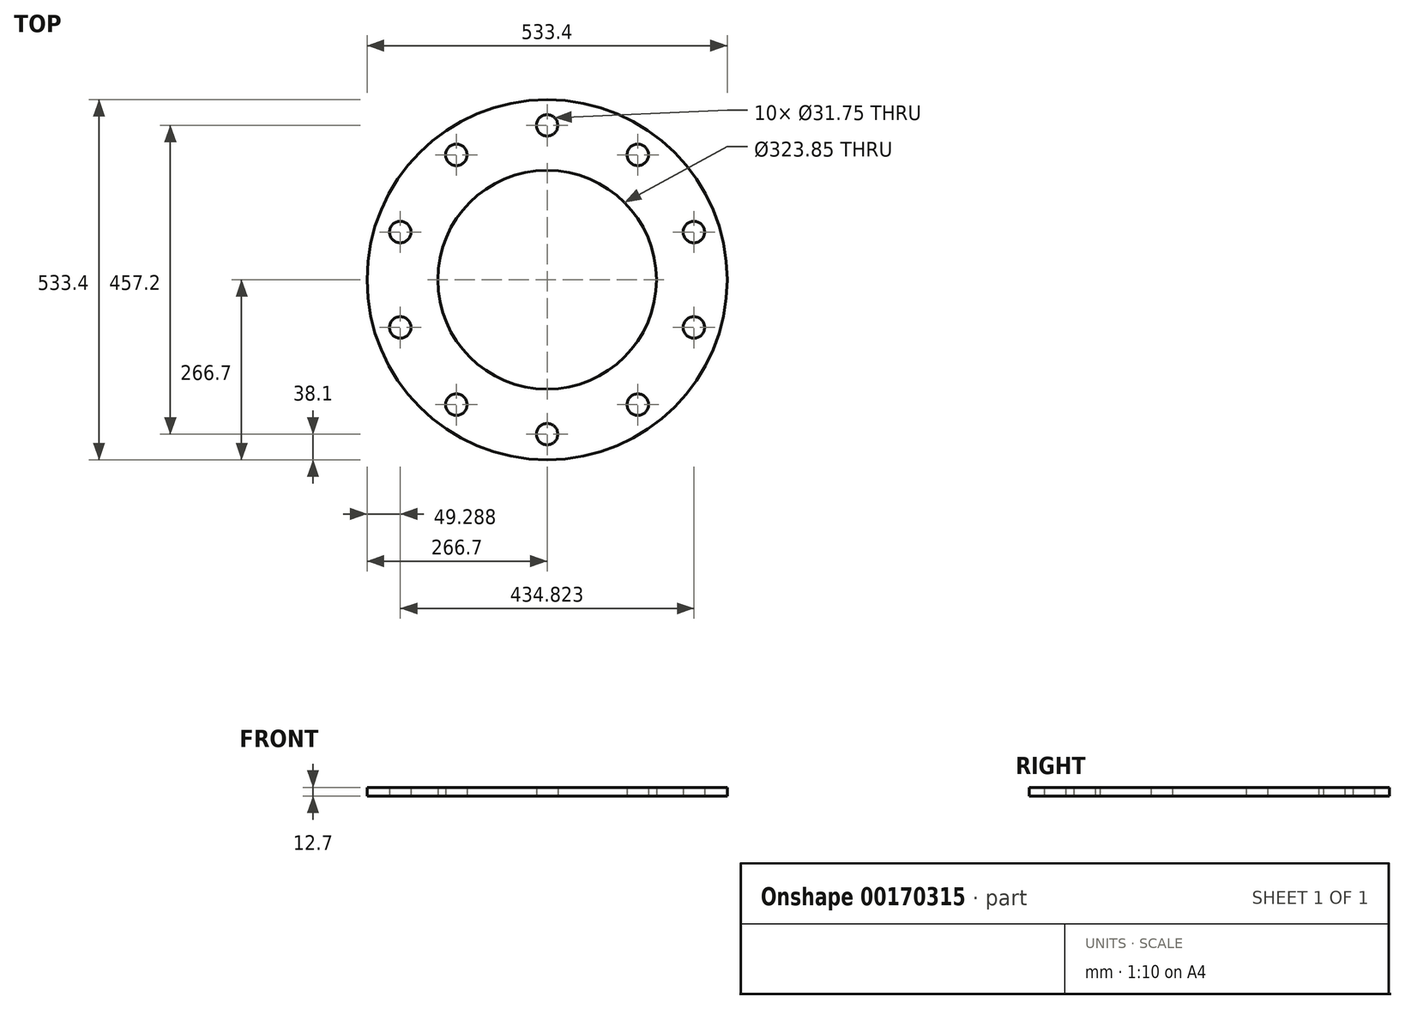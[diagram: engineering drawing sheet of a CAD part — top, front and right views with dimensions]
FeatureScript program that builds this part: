
annotation { "Feature Type Name" : "Feature", "Feature Type Description" : "" }
export const myFeature = defineFeature(function(context is Context, id is Id, definition is map)
    precondition{}
    {
        {
            var Q0;
            Q0=qCreatedBy(makeId("Top.planeOp"),FACE);
            var sketch = newSketch(context, id + "F0", { "sketchPlane" : qUnion([Q0])});
            skCircle(sketch, "E0", {"center": v(0, 0) * mm, "radius": 161.93 * mm});
            skCircle(sketch, "E1", {"center": v(0, 0) * mm, "radius": 266.7 * mm});
            skSolve(sketch);
        }
        {
            var Q0;
            Q0=makeQuery(id+"F0.imprint","IMPRINT",FACE,{"disambiguationData":[TD([[makeQuery(id+"F0.imprint","IMPRINT",EDGE,{"derivedFrom":sQuery(id+"F0.wireOp",EDGE,"E0")}),-1.0]])]});
            extrude(context, id + "F1", {"entities" : qUnion([Q0]), "depth" : 12.7 * mm});
        }
        {
            var Q0;
            Q0=qCreatedBy(makeId("Top.planeOp"),FACE);
            var sketch = newSketch(context, id + "F2", { "sketchPlane" : qUnion([Q0])});
            skCircle(sketch, "E2", {"center": v(0, 0) * mm, "radius": 228.6 * mm, "construction": true});
            skCircle(sketch, "E3", {"center": v(0, 228.6) * mm, "radius": 15.88 * mm});
            skCircle(sketch, "E4.1.0", {"center": v(-134.37, 184.94) * mm, "radius": 15.88 * mm});
            skCircle(sketch, "E4.2.0", {"center": v(-217.41, 70.64) * mm, "radius": 15.88 * mm});
            skCircle(sketch, "E4.3.0", {"center": v(-217.41, -70.64) * mm, "radius": 15.88 * mm});
            skCircle(sketch, "E4.4.0", {"center": v(-134.37, -184.94) * mm, "radius": 15.88 * mm});
            skCircle(sketch, "E4.5.0", {"center": v(0, -228.6) * mm, "radius": 15.88 * mm});
            skCircle(sketch, "E4.6.0", {"center": v(134.37, -184.94) * mm, "radius": 15.88 * mm});
            skCircle(sketch, "E4.7.0", {"center": v(217.41, -70.64) * mm, "radius": 15.88 * mm});
            skCircle(sketch, "E4.8.0", {"center": v(217.41, 70.64) * mm, "radius": 15.88 * mm});
            skCircle(sketch, "E4.9.0", {"center": v(134.37, 184.94) * mm, "radius": 15.88 * mm});
            skSolve(sketch);
        }
        {
            var Q0;
            Q0 = qSketchRegion(id + "F2", true);
            extrude(context, id + "F3", {"entities" : qUnion([Q0]), "operationType" : NewBodyOperationType.REMOVE, "depth" : 15.88 * mm});
        }
    });
